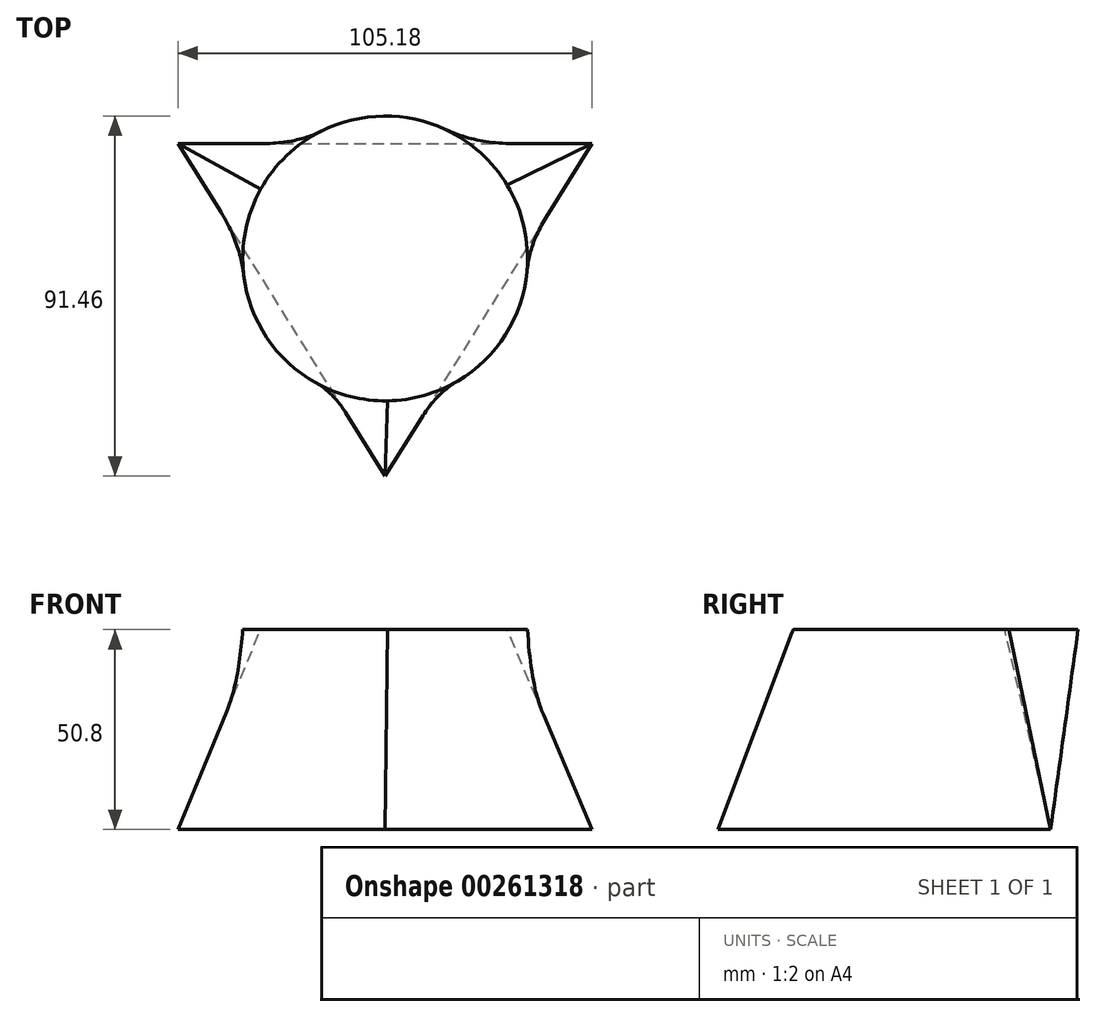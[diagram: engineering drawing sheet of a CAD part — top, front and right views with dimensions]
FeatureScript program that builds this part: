
annotation { "Feature Type Name" : "Feature", "Feature Type Description" : "" }
export const myFeature = defineFeature(function(context is Context, id is Id, definition is map)
    precondition{}
    {
        {
            var Q0;
            Q0=qCreatedBy(makeId("Top.planeOp"),FACE);
            var sketch = newSketch(context, id + "F0", { "sketchPlane" : qUnion([Q0])});
            skCircle(sketch, "E0", {"center": v(0, 0) * mm, "radius": 29.2 * mm, "construction": true});
            skLineSegment(sketch, "E1", {"start": v(-52.59, 29.21) * mm, "end": v(52.59, 29.21) * mm});
            skLineSegment(sketch, "E2", {"start": v(52.59, 29.2) * mm, "end": v(0, -55.28) * mm});
            skLineSegment(sketch, "E3", {"start": v(0, -55.28) * mm, "end": v(-52.59, 29.2) * mm});
            skSolve(sketch);
        }
        {
            var Q0;
            Q0=makeQuery(id+"F0.imprint","IMPRINT",FACE,{"disambiguationData":[TD([[makeQuery(id+"F0.imprint","IMPRINT",EDGE,{"derivedFrom":sQuery(id+"F0.wireOp",EDGE,"E1")}),-1.0]])]});
            cPlane(context, id + "F1", {"entities" : qUnion([Q0]), "cplaneType" : CPlaneType.OFFSET, "offset" : 50.8 * mm, "width" : 152.4 * mm, "height" : 152.4 * mm});
        }
        {
            var Q0;
            Q0=qCreatedBy(id+"F1.planeOp",FACE);
            var sketch = newSketch(context, id + "F2", { "sketchPlane" : qUnion([Q0])});
            skCircle(sketch, "E4", {"center": v(0, 0) * mm, "radius": 36.18 * mm});
            skSolve(sketch);
        }
        {
            var Q0;
            Q0=makeQuery(id+"F0.imprint","IMPRINT",FACE,{"disambiguationData":[TD([[makeQuery(id+"F0.imprint","IMPRINT",EDGE,{"derivedFrom":sQuery(id+"F0.wireOp",EDGE,"E1")}),-1.0]])]});
            var Q1;
            Q1=makeQuery(id+"F2.imprint","IMPRINT",FACE,{"disambiguationData":[TD([[makeQuery(id+"F2.imprint","IMPRINT",EDGE,{"derivedFrom":sQuery(id+"F2.wireOp",EDGE,"E4")}),1.0]])]});
            loft(context, id + "F3", {"sheetProfilesArray" : [{ "sheetProfileEntities" : qUnion([Q0]) }, { "sheetProfileEntities" : qUnion([Q1]) }]});
        }
    });
